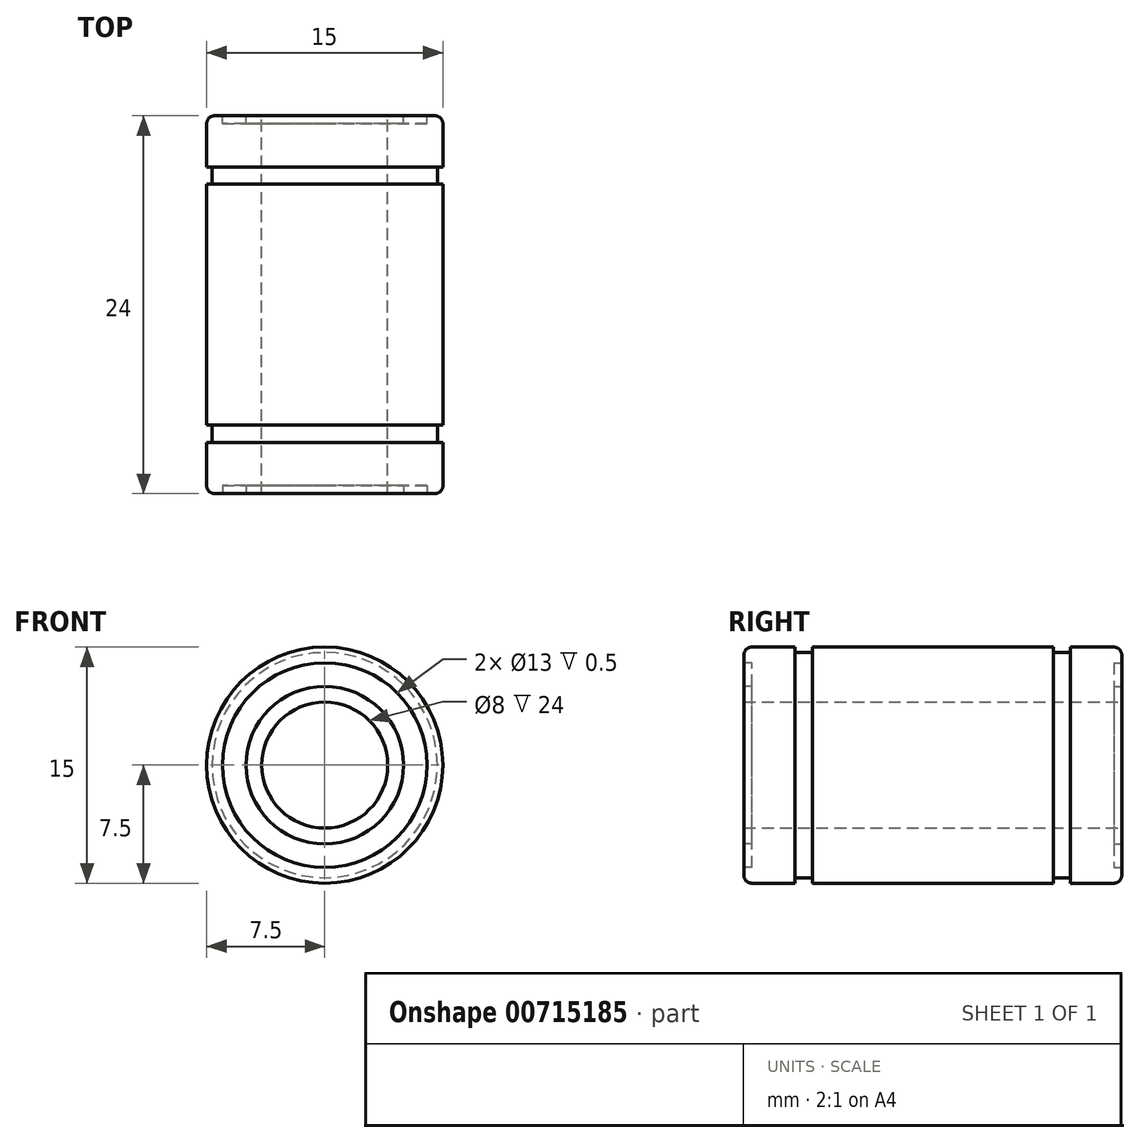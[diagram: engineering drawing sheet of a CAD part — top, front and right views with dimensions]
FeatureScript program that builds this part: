
annotation { "Feature Type Name" : "Feature", "Feature Type Description" : "" }
export const myFeature = defineFeature(function(context is Context, id is Id, definition is map)
    precondition{}
    {
        {
            var Q0;
            Q0=qCreatedBy(makeId("Front.planeOp"),FACE);
            var sketch = newSketch(context, id + "F0", { "sketchPlane" : qUnion([Q0])});
            skCircle(sketch, "E0", {"center": v(0, 0) * mm, "radius": 4 * mm});
            skCircle(sketch, "E1", {"center": v(0, 0) * mm, "radius": 7.5 * mm});
            skSolve(sketch);
        }
        {
            var Q0;
            Q0 = qSketchRegion(id + "F0", true);
            extrude(context, id + "F1", {"entities" : qUnion([Q0]), "endBound" : BoundingType.SYMMETRIC, "depth" : 24 * mm, "offsetDistance" : 25 * mm});
        }
        {
            var Q0;
            Q0=qCreatedBy(makeId("Top.planeOp"),FACE);
            var sketch = newSketch(context, id + "F2", { "sketchPlane" : qUnion([Q0])});
            skLineSegment(sketch, "E2", {"start": v(0, 0) * mm, "end": v(0, 20.67) * mm, "construction": true});
            skLineSegment(sketch, "E3.bottom", {"start": v(-8.15, 8.75) * mm, "end": v(-7.15, 8.75) * mm});
            skLineSegment(sketch, "E3.top", {"start": v(-8.15, 7.65) * mm, "end": v(-7.15, 7.65) * mm});
            skLineSegment(sketch, "E3.left", {"start": v(-8.15, 8.75) * mm, "end": v(-8.15, 7.65) * mm});
            skLineSegment(sketch, "E3.right", {"start": v(-7.15, 8.75) * mm, "end": v(-7.15, 7.65) * mm});
            skLineSegment(sketch, "E4.bottom", {"start": v(-8.15, -7.65) * mm, "end": v(-7.15, -7.65) * mm});
            skLineSegment(sketch, "E4.top", {"start": v(-8.15, -8.75) * mm, "end": v(-7.15, -8.75) * mm});
            skLineSegment(sketch, "E4.left", {"start": v(-8.15, -7.65) * mm, "end": v(-8.15, -8.75) * mm});
            skLineSegment(sketch, "E4.right", {"start": v(-7.15, -7.65) * mm, "end": v(-7.15, -8.75) * mm});
            skLineSegment(sketch, "E5", {"start": v(0, 0) * mm, "end": v(-12.61, 0) * mm, "construction": true});
            skSolve(sketch);
        }
        {
            var Q0;
            Q0 = qSketchRegion(id + "F2", true);
            var Q1;
            Q1=sQuery(id+"F2.wireOp",EDGE,"E2");
            revolve(context, id + "F3", {"operationType" : NewBodyOperationType.REMOVE, "surfaceOperationType" : NewSurfaceOperationType.NEW, "entities" : qUnion([Q0]), "axis" : qUnion([Q1]), "revolveType" : RevolveType.FULL, "oppositeDirection" : true});
        }
        {
            var Q0;
            Q0=makeQuery(id+"F1.opExtrude","CAP_FACE",FACE,{"disambiguationData":[OSD([sQuery(id+"F0.wireOp",EDGE,"E0"),sQuery(id+"F0.wireOp",EDGE,"E1")])],"isStart":false});
            var sketch = newSketch(context, id + "F4", { "sketchPlane" : qUnion([Q0])});
            skCircle(sketch, "E6", {"center": v(0, 0) * mm, "radius": 5 * mm});
            skCircle(sketch, "E7", {"center": v(0, 0) * mm, "radius": 6.5 * mm});
            skSolve(sketch);
        }
        {
            var Q0;
            Q0 = qSketchRegion(id + "F4", true);
            extrude(context, id + "F5", {"entities" : qUnion([Q0]), "operationType" : NewBodyOperationType.REMOVE, "oppositeDirection" : true, "depth" : .5 * mm, "offsetDistance" : 25 * mm});
        }
        {
            var Q0;
            Q0=makeQuery(id+"F1.opExtrude","CAP_FACE",FACE,{"disambiguationData":[OSD([sQuery(id+"F0.wireOp",EDGE,"E0"),sQuery(id+"F0.wireOp",EDGE,"E1")])],"isStart":true});
            var sketch = newSketch(context, id + "F6", { "sketchPlane" : qUnion([Q0])});
            skCircle(sketch, "E8", {"center": v(0, 0) * mm, "radius": 5 * mm});
            skCircle(sketch, "E9", {"center": v(0, 0) * mm, "radius": 6.5 * mm});
            skSolve(sketch);
        }
        {
            var Q0;
            Q0 = qSketchRegion(id + "F6", true);
            extrude(context, id + "F7", {"entities" : qUnion([Q0]), "operationType" : NewBodyOperationType.REMOVE, "oppositeDirection" : true, "depth" : .5 * mm, "offsetDistance" : 25 * mm});
        }
        {
            var Q0;
            Q0=makeQuery(id+"F1.opExtrude","CAP_EDGE",EDGE,{"disambiguationData":[OSD([sQuery(id+"F0.wireOp",EDGE,"E1")])],"isStart":true});
            var Q1;
            Q1=makeQuery(id+"F1.opExtrude","CAP_EDGE",EDGE,{"disambiguationData":[OSD([sQuery(id+"F0.wireOp",EDGE,"E1")])],"isStart":false});
            fillet(context, id + "F8", {"entities" : qUnion([Q0, Q1]), "radius" : .5 * mm, "tangentPropagation" : true, "allowEdgeOverflow" : false});
        }
    });
